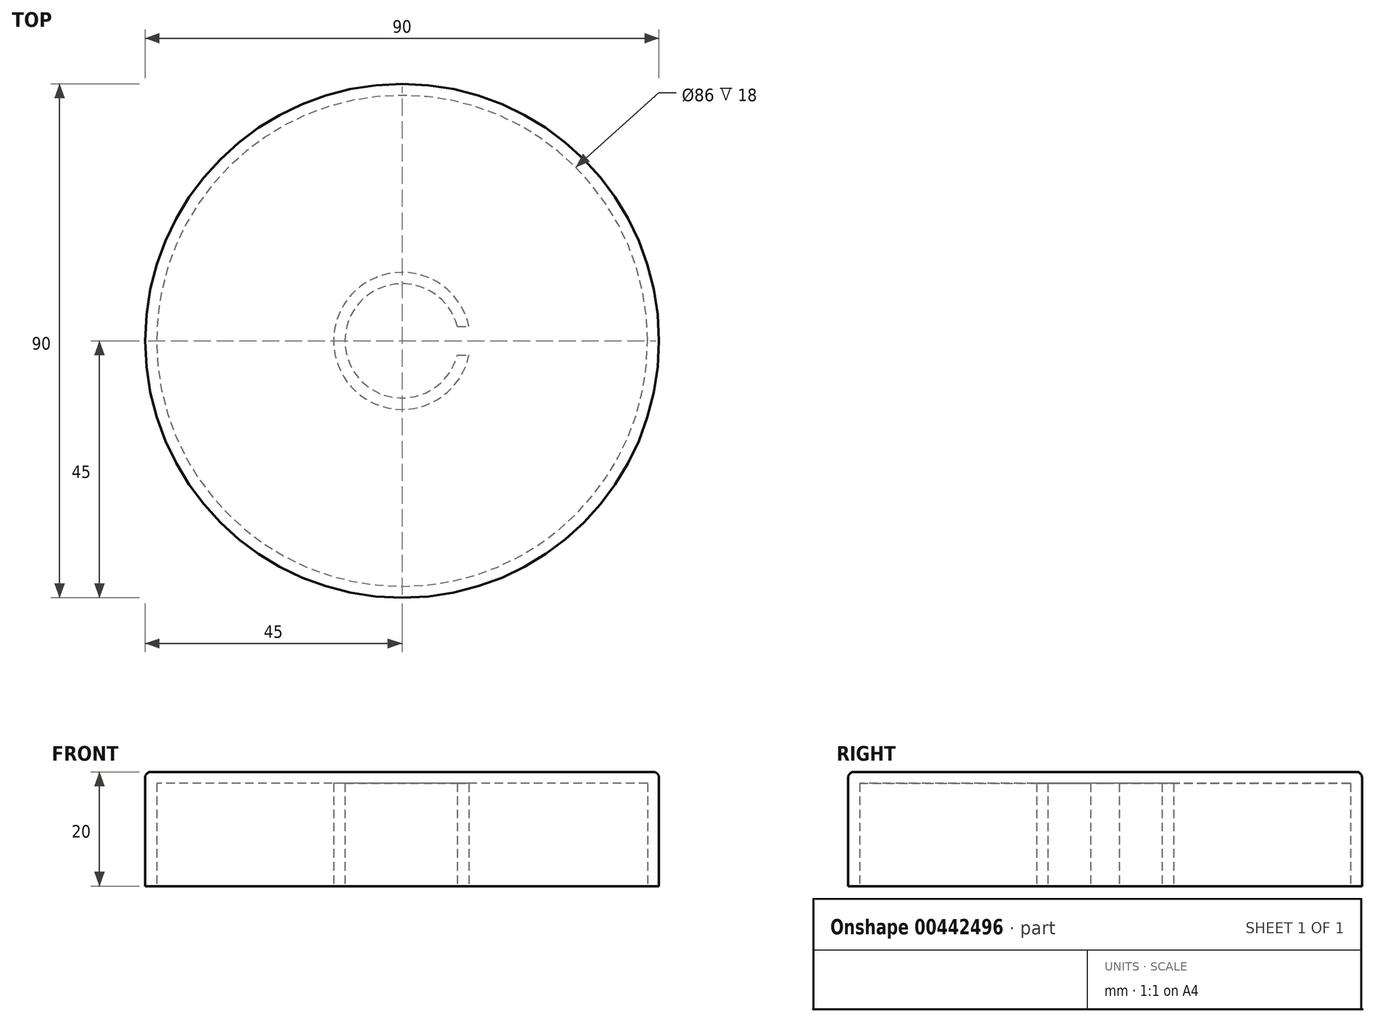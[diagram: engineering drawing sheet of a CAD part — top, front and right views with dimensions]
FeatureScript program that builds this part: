
annotation { "Feature Type Name" : "Feature", "Feature Type Description" : "" }
export const myFeature = defineFeature(function(context is Context, id is Id, definition is map)
    precondition{}
    {
        {
            var Q0;
            Q0=qCreatedBy(makeId("Top.planeOp"),FACE);
            var sketch = newSketch(context, id + "F0", { "sketchPlane" : qUnion([Q0])});
            skCircle(sketch, "E0", {"center": v(0, 0) * mm, "radius": 45 * mm});
            skSolve(sketch);
        }
        {
            var Q0;
            Q0 = qSketchRegion(id + "F0", true);
            extrude(context, id + "F1", {"entities" : qUnion([Q0]), "depth" : 20 * mm});
        }
        {
            var Q0;
            Q0=makeQuery(id+"F1.opExtrude","CAP_FACE",FACE,{"disambiguationData":[OSD([sQuery(id+"F0.wireOp",EDGE,"E0")])],"isStart":true});
            shell(context, id + "F2", {"entities" : qUnion([Q0]), "thickness" : 2 * mm});
        }
        {
            var Q0;
            Q0=qCreatedBy(makeId("Top.planeOp"),FACE);
            var sketch = newSketch(context, id + "F3", { "sketchPlane" : qUnion([Q0])});
            skCircle(sketch, "E1", {"center": v(0, 0) * mm, "radius": 12 * mm});
            skSolve(sketch);
        }
        {
            var Q0;
            Q0=makeQuery(id+"F3.imprint","IMPRINT",FACE,{"disambiguationData":[TD([[makeQuery(id+"F3.imprint","IMPRINT",EDGE,{"derivedFrom":sQuery(id+"F3.wireOp",EDGE,"E1")}),1.0]])]});
            var Q1;
            Q1=sQuery(id+"F3.wireOp",EDGE,"E1");
            extrude(context, id + "F4", {"entities" : qUnion([Q0]), "operationType" : NewBodyOperationType.ADD, "surfaceEntities" : qUnion([Q1]), "endBound" : BoundingType.UP_TO_NEXT, "depth" : 25 * mm});
        }
        {
            var Q0;
            Q0=makeQuery(id+"F4.opExtrude","CAP_FACE",FACE,{"disambiguationData":[OSD([sQuery(id+"F3.wireOp",EDGE,"E1")])],"isStart":true});
            shell(context, id + "F5", {"entities" : qUnion([Q0]), "thickness" : 2 * mm});
        }
        {
            var Q0;
            Q0=makeQuery(id+"F4.opExtrude","CAP_FACE",FACE,{"disambiguationData":[OSD([sQuery(id+"F3.wireOp",EDGE,"E1")])],"isStart":true});
            var sketch = newSketch(context, id + "F6", { "sketchPlane" : qUnion([Q0])});
            skLineSegment(sketch, "E2.top", {"start": v(2.35, -2.5) * mm, "end": v(13.94, -2.5) * mm});
            skLineSegment(sketch, "E2.left", {"start": v(2.35, 0) * mm, "end": v(2.35, -2.5) * mm});
            skLineSegment(sketch, "E2.right", {"start": v(13.94, 0) * mm, "end": v(13.94, -2.5) * mm});
            skLineSegment(sketch, "E3.MirrorCS", {"start": v(2.35, 0) * mm, "end": v(2.35, 2.5) * mm});
            skLineSegment(sketch, "E4.MirrorCS", {"start": v(2.35, 2.5) * mm, "end": v(13.94, 2.5) * mm});
            skLineSegment(sketch, "E5.MirrorCS", {"start": v(13.94, 0) * mm, "end": v(13.94, 2.5) * mm});
            skSolve(sketch);
        }
        {
            var Q0;
            {var subQ0=sQuery(id+"F6.wireOp",EDGE,"E2.top");var subQ1=sQuery(id+"F3.wireOp",EDGE,"E1");var subQ2=makeQuery(id+"F4.opExtrude","CAP_EDGE",EDGE,{"disambiguationData":[OSD([subQ1])],"isStart":true});var subQ3=makeQuery(id+"F6.imprint","INTERSECT",VERTEX,{"derivedFrom":[subQ2,subQ0]});Q0=makeQuery(id+"F6.imprint","IMPRINT",FACE,{"disambiguationData":[TD([[makeQuery(id+"F6.imprint","IMPRINT",EDGE,{"disambiguationData":[TD([[subQ3,1.0]])],"derivedFrom":subQ0}),1.0]])]});}
            var Q1;
            {var subQ0=sQuery(id+"F0.wireOp",EDGE,"E0");Q1=makeQuery(id+"F2.opShell","OFFSET_FACE",FACE,{"disambiguationData":[OSD([subQ0]),TDD([makeQuery(id+"F1.opExtrude","CAP_FACE",FACE,{"disambiguationData":[OSD([subQ0])],"isStart":false})])]});}
            extrude(context, id + "F7", {"entities" : qUnion([Q0]), "operationType" : NewBodyOperationType.REMOVE, "endBound" : BoundingType.UP_TO_SURFACE, "oppositeDirection" : true, "endBoundEntityFace" : qUnion([Q1]), "depth" : 25 * mm});
        }
        {
            var Q0;
            Q0=makeQuery(id+"F1.opExtrude","CAP_EDGE",EDGE,{"disambiguationData":[OSD([sQuery(id+"F0.wireOp",EDGE,"E0")])],"isStart":false});
            fillet(context, id + "F8", {"entities" : qUnion([Q0]), "radius" : 1 * mm, "tangentPropagation" : true, "allowEdgeOverflow" : false});
        }
    });
